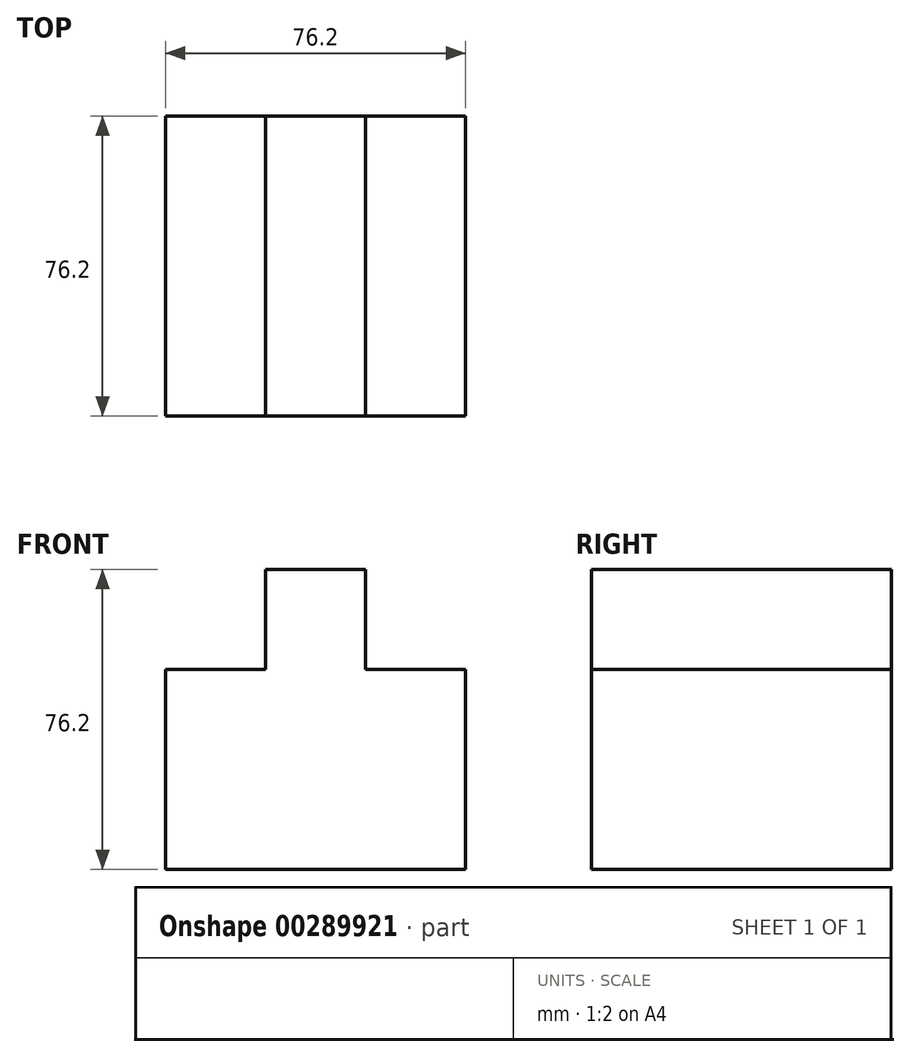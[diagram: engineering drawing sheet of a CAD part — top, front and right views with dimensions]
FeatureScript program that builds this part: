
annotation { "Feature Type Name" : "Feature", "Feature Type Description" : "" }
export const myFeature = defineFeature(function(context is Context, id is Id, definition is map)
    precondition{}
    {
        {
            var Q0;
            Q0=qCreatedBy(makeId("Front.planeOp"),FACE);
            var sketch = newSketch(context, id + "F0", { "sketchPlane" : qUnion([Q0])});
            skLineSegment(sketch, "E0", {"start": v(0, 0) * mm, "end": v(-76.2, 0) * mm});
            skLineSegment(sketch, "E1", {"start": v(-76.2, 50.8) * mm, "end": v(-76.2, 0) * mm});
            skLineSegment(sketch, "E2", {"start": v(-76.2, 50.8) * mm, "end": v(-50.8, 50.8) * mm});
            skLineSegment(sketch, "E3", {"start": v(-50.8, 50.8) * mm, "end": v(-50.8, 76.2) * mm});
            skLineSegment(sketch, "E4", {"start": v(-50.8, 76.2) * mm, "end": v(-25.4, 76.2) * mm});
            skLineSegment(sketch, "E5", {"start": v(-25.4, 76.2) * mm, "end": v(-25.4, 50.8) * mm});
            skLineSegment(sketch, "E6", {"start": v(-25.4, 50.8) * mm, "end": v(0, 50.8) * mm});
            skLineSegment(sketch, "E7", {"start": v(0, 50.8) * mm, "end": v(0, 0) * mm});
            skSolve(sketch);
        }
        {
            var Q0;
            Q0=makeQuery(id+"F0.imprint","IMPRINT",FACE,{"disambiguationData":[TD([[makeQuery(id+"F0.imprint","IMPRINT",EDGE,{"derivedFrom":sQuery(id+"F0.wireOp",EDGE,"E0")}),-1.0]])]});
            extrude(context, id + "F1", {"entities" : qUnion([Q0]), "depth" : 76.2 * mm});
        }
    });
